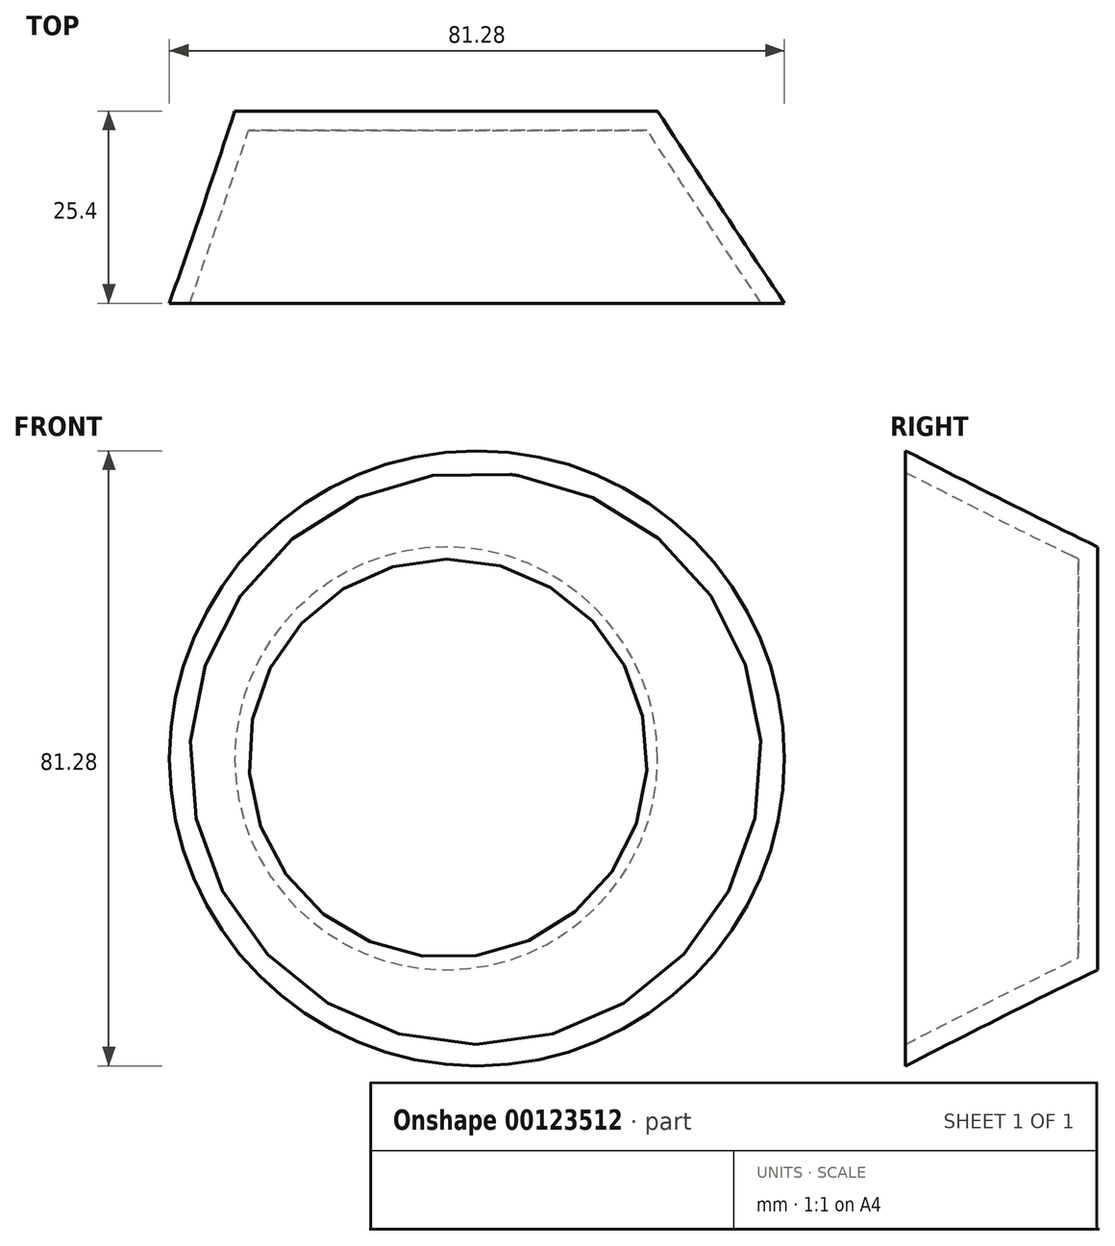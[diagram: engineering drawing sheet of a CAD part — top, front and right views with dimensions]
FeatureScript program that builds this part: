
annotation { "Feature Type Name" : "Feature", "Feature Type Description" : "" }
export const myFeature = defineFeature(function(context is Context, id is Id, definition is map)
    precondition{}
    {
        {
            var Q0;
            Q0=qCreatedBy(makeId("Front.planeOp"),FACE);
            var sketch = newSketch(context, id + "F0", { "sketchPlane" : qUnion([Q0])});
            skCircle(sketch, "E0", {"center": v(0, 0) * mm, "radius": 27.94 * mm});
            skSolve(sketch);
        }
        {
            var Q0;
            Q0=qCreatedBy(makeId("Front.planeOp"),FACE);
            cPlane(context, id + "F1", {"entities" : qUnion([Q0]), "cplaneType" : CPlaneType.OFFSET, "offset" : 25.4 * mm, "width" : 152.4 * mm, "height" : 152.4 * mm});
        }
        {
            var Q0;
            Q0=qCreatedBy(id+"F1.planeOp",FACE);
            var sketch = newSketch(context, id + "F2", { "sketchPlane" : qUnion([Q0])});
            skCircle(sketch, "E1", {"center": v(4.06, 0) * mm, "radius": 40.64 * mm});
            skSolve(sketch);
        }
        {
            var Q0;
            Q0=makeQuery(id+"F0.imprint","IMPRINT",FACE,{"disambiguationData":[TD([[makeQuery(id+"F0.imprint","IMPRINT",EDGE,{"derivedFrom":sQuery(id+"F0.wireOp",EDGE,"E0")}),1.0]])]});
            var Q1;
            Q1=makeQuery(id+"F2.imprint","IMPRINT",FACE,{"disambiguationData":[TD([[makeQuery(id+"F2.imprint","IMPRINT",EDGE,{"derivedFrom":sQuery(id+"F2.wireOp",EDGE,"E1")}),1.0]])]});
            loft(context, id + "F3", {"sheetProfilesArray" : [{ "sheetProfileEntities" : qUnion([Q0]) }, { "sheetProfileEntities" : qUnion([Q1]) }]});
        }
        {
            var Q0;
            Q0=makeQuery(id+"F3.opLoft","CAP_FACE",FACE,{"disambiguationData":[OSD([makeQuery(id+"F2.imprint","IMPRINT",FACE,{"disambiguationData":[TD([[makeQuery(id+"F2.imprint","IMPRINT",EDGE,{"derivedFrom":sQuery(id+"F2.wireOp",EDGE,"E1")}),1.0]])]})])],"isStart":true});
            shell(context, id + "F4", {"entities" : qUnion([Q0]), "thickness" : 2.54 * mm});
        }
    });
